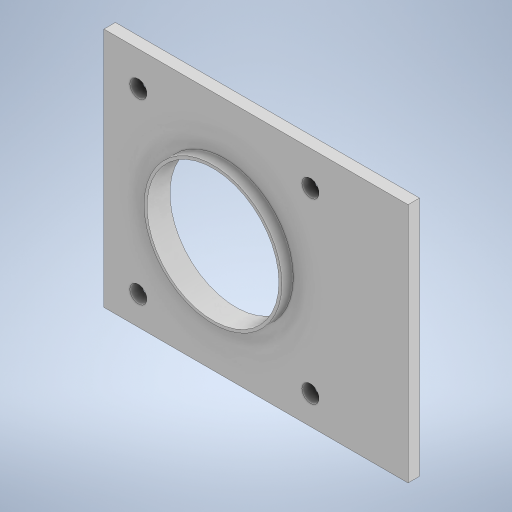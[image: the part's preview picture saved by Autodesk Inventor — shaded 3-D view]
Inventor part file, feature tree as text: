
AUTODESK INVENTOR PART (.ipt)
format: ipt  version: 2024 (Build 280153000, 153)  size: 588,288 bytes
history: native  units: mm
features: extrude x2, sketch x2, projected_geometry x1
ambient origin geometry x8: Origin, YZ Plane, XZ Plane, XY Plane, X Axis, Y Axis, Z Axis, Center Point
bodies: Solid1 (feature_tree)
feature tree (5):
  extrude  "Extrusion1"  Depth=32.0mm
  extrude  "Extrusion2"  Depth=42.0mm
  sketch  "Sketch1"  dims[d0=32.0mm d1=24.0mm]
  sketch  "Sketch2"  dims[d2=42.0mm d3=42.0mm d4=3.0mm d5=3.0mm d6=31.0mm d7=15.0mm d8=15.0mm d9=2.0mm d10=0.0mm d11=23.0mm d12=4.0mm d13=0.0mm d14=11.0mm]
  projected_geometry  "Projected Loop1"
